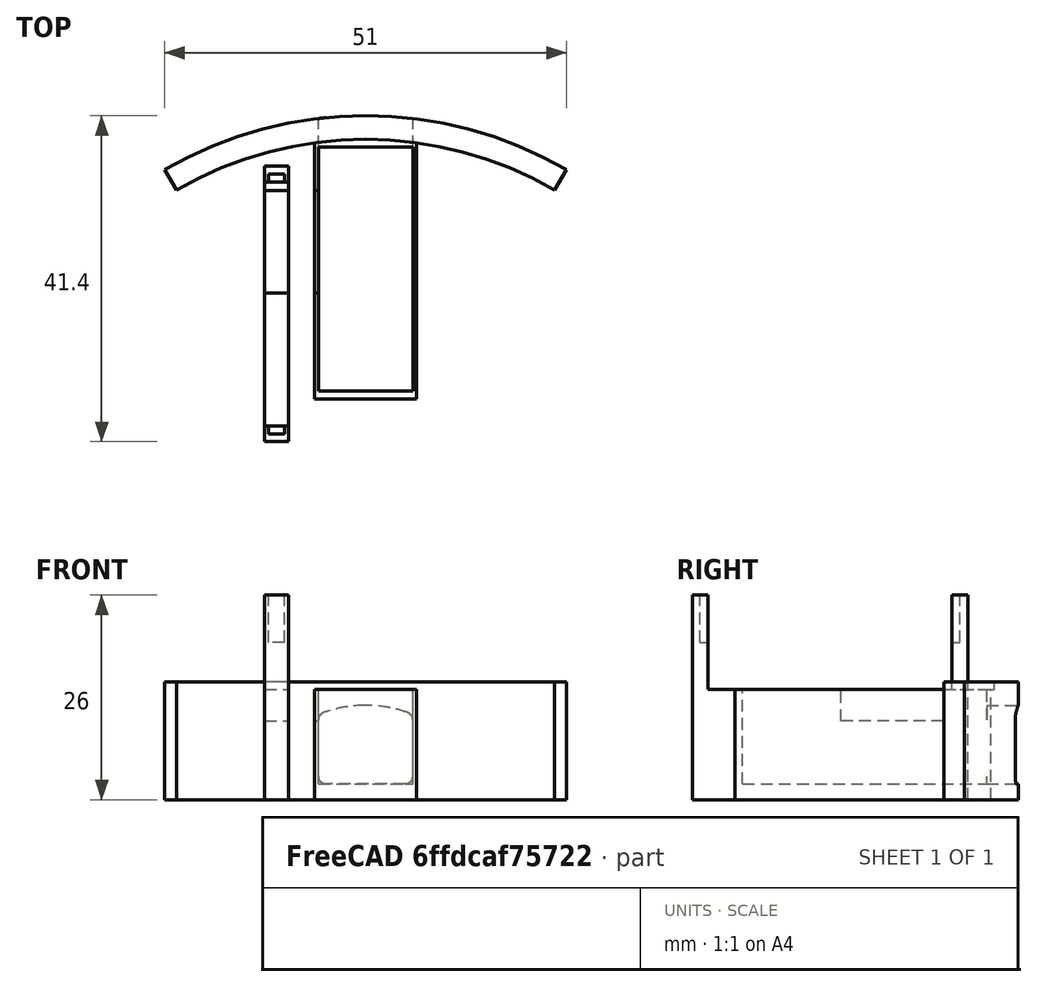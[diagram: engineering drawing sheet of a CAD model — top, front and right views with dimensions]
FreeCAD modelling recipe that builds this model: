
FCSTD DOCUMENT  (FreeCAD 0.16R4924 (Git))
Label: interior_servo_bay_v4p1
License: All rights reserved
LicenseURL: http://en.wikipedia.org/wiki/All_rights_reserved
objects: Part::Cut×6, Part::Box×6, Part::MultiFuse×3, Part::Cylinder×2, Part::Feature×2, Part::Extrusion×2, App::MeasureDistance×2, Part::Thickness×1
note: 22 computed .brp shape members not serialized (recipe doc carries the construction recipe); baked Part::Feature solids carry a one-line shape summary decoded from their .brp

FEATURE [Part::Cylinder] Cylinder  label="bottle_wall"
  Angle = 60
  Height = 15
  Placement = pos=(8.5,-7,0) rot=(0,0,1;1.0472rad)
  Radius = 51
FEATURE [Part::Cylinder] Cylinder001  label="bottle_wall001"
  Angle = 60
  Height = 15
  Placement = pos=(8.5,-7,0) rot=(0,0,1;1.0472rad)
  Radius = 48
FEATURE [Part::Cut] Cut  label="bottle_wall_composite"
  Base = -> Cylinder
  Placement = pos=(0,-2,0) rot=(0,0,1;0rad)
  Tool = -> Cylinder001
FEATURE [Part::Feature] Common_cs  label="pin_cs"
  Placement = pos=(3.5,35,2) rot=(0,0,1;0rad)
  shape: bbox 10 x 2e-07 x 8 mm, 0 faces, 0 solids (baked)
FEATURE [Part::Extrusion] Extrude
  Base = -> Common_cs
  Dir = (0,5,0)
  Solid = true
FEATURE [Part::Thickness] Thickness
  Faces = -> Extrude [Face7]
  Intersection = false
  Join = 0
  Mode = 0
  SelfIntersection = false
  Value = 1
FEATURE [Part::Feature] Common_cs001  label="pin_cs001"
  Placement = pos=(3.5,35,2) rot=(0,0,1;0rad)
  shape: bbox 10 x 2e-07 x 8 mm, 0 faces, 0 solids (baked)
FEATURE [Part::Extrusion] Extrude001
  Base = -> Common_cs001
  Dir = (0,5,0)
  Solid = true
FEATURE [Part::MultiFuse] Fusion  label="bolt_bottle_side_opening"
  Placement = pos=(0,-7,1) rot=(0,0,1;0rad)
  Shapes = -> [Thickness,Extrude,Extrude001]
FEATURE [Part::Box] Box  label="pullBay"
  Height = 15
  Length = 12
  Placement = pos=(2.5,7,2) rot=(0,0,1;0rad)
  Width = 31
FEATURE [Part::Box] Box001  label="Case"
  Height = 14
  Length = 13
  Placement = pos=(2,6,0) rot=(0,0,1;0rad)
  Width = 34
FEATURE [Part::Cut] Cut001  label="cut bay from case"
  Base = -> Box001
  Tool = -> Box
FEATURE [Part::MultiFuse] Fusion001  label="wall plus case"
  Shapes = -> [Cut,Cut001]
FEATURE [Part::Cut] Cut002  label="hole cut out of case"
  Base = -> Fusion001
  Tool = -> Fusion
FEATURE [Part::Box] Box002  label="slot wall"
  Height = 26
  Length = 3
  Placement = pos=(-1,5,0) rot=(0,0,1;0rad)
  Width = 35
FEATURE [Part::Box] Box003  label="slot wall cutout1"
  Height = 11.2
  Length = 2
  Placement = pos=(-0.5,6,20) rot=(0,0,1;0rad)
  Width = 33
FEATURE [Part::Cut] Cut003
  Base = -> Box002
  Tool = -> Box003
FEATURE [Part::Box] Box004  label="slot wall cutout2"
  Height = 14
  Length = 3
  Placement = pos=(-1,7,14) rot=(0,0,1;0rad)
  Width = 31
FEATURE [Part::Cut] Cut004  label="wall slot finished"
  Base = -> Cut003
  Placement = pos=(-3.3,-4.4,0) rot=(0,0,1;0rad)
  Tool = -> Box004
FEATURE [Part::MultiFuse] Fusion002
  Shapes = -> [Cut002,Cut004]
FEATURE [App::MeasureDistance] Distance  label="Distance: 33.123"
  Distance = 33.1232
  P1 = (1.15787,39.1229,26)
  P2 = (1.00961,6,26)
FEATURE [App::MeasureDistance] Distance001  label="Distance: 12.028"
  Distance = 12.0279
  P1 = (0,7,26)
  P2 = (0,7.81869,14)
FEATURE [Part::Box] Box005  label="servo wall cutaway"
  Height = 4
  Length = 10
  Placement = pos=(-6,19.5,10) rot=(0,0,1;0rad)
  Width = 13
FEATURE [Part::Cut] Cut005
  Base = -> Fusion002
  Tool = -> Box005
